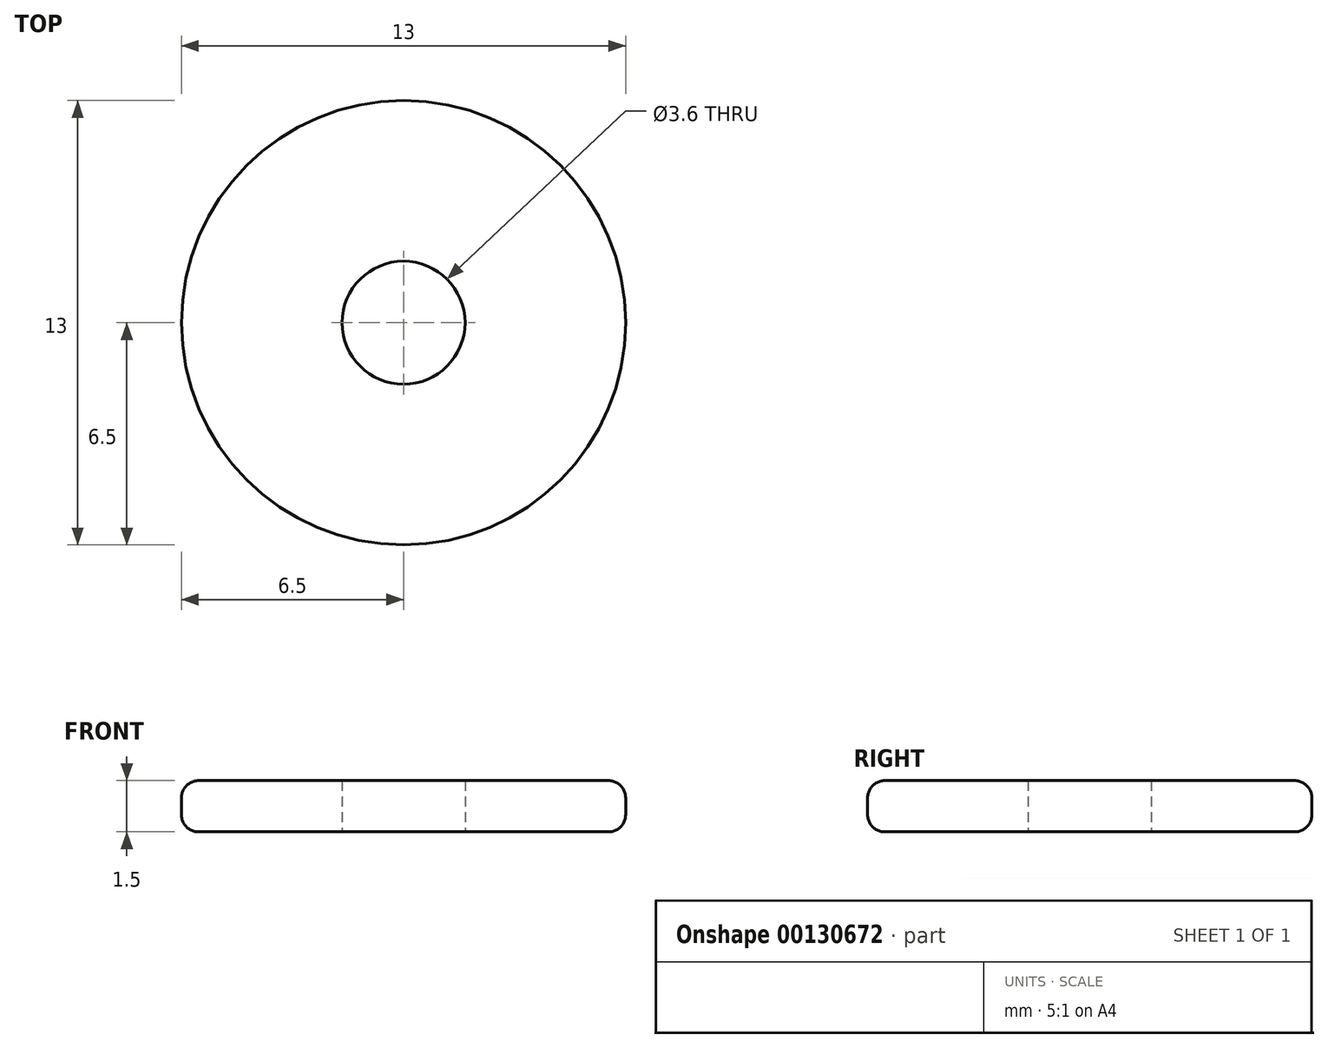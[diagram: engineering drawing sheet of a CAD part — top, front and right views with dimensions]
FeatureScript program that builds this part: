
annotation { "Feature Type Name" : "Feature", "Feature Type Description" : "" }
export const myFeature = defineFeature(function(context is Context, id is Id, definition is map)
    precondition{}
    {
        {
            var Q0;
            Q0=qCreatedBy(makeId("Top.planeOp"),FACE);
            var sketch = newSketch(context, id + "F0", { "sketchPlane" : qUnion([Q0])});
            skCircle(sketch, "E0", {"center": v(0, 0) * mm, "radius": 6.5 * mm});
            skCircle(sketch, "E1", {"center": v(0, 0) * mm, "radius": 1.8 * mm});
            skSolve(sketch);
        }
        {
            var Q0;
            Q0 = qSketchRegion(id + "F0", true);
            extrude(context, id + "F1", {"entities" : qUnion([Q0]), "depth" : 1.5 * mm});
        }
        {
            var Q0;
            Q0=makeQuery(id+"F1.opExtrude","CAP_EDGE",EDGE,{"disambiguationData":[OSD([sQuery(id+"F0.wireOp",EDGE,"E0")])],"isStart":false});
            var Q1;
            Q1=makeQuery(id+"F1.opExtrude","CAP_EDGE",EDGE,{"disambiguationData":[OSD([sQuery(id+"F0.wireOp",EDGE,"E0")])],"isStart":true});
            fillet(context, id + "F2", {"entities" : qUnion([Q0, Q1]), "radius" : .5 * mm, "tangentPropagation" : true, "allowEdgeOverflow" : false});
        }
    });
